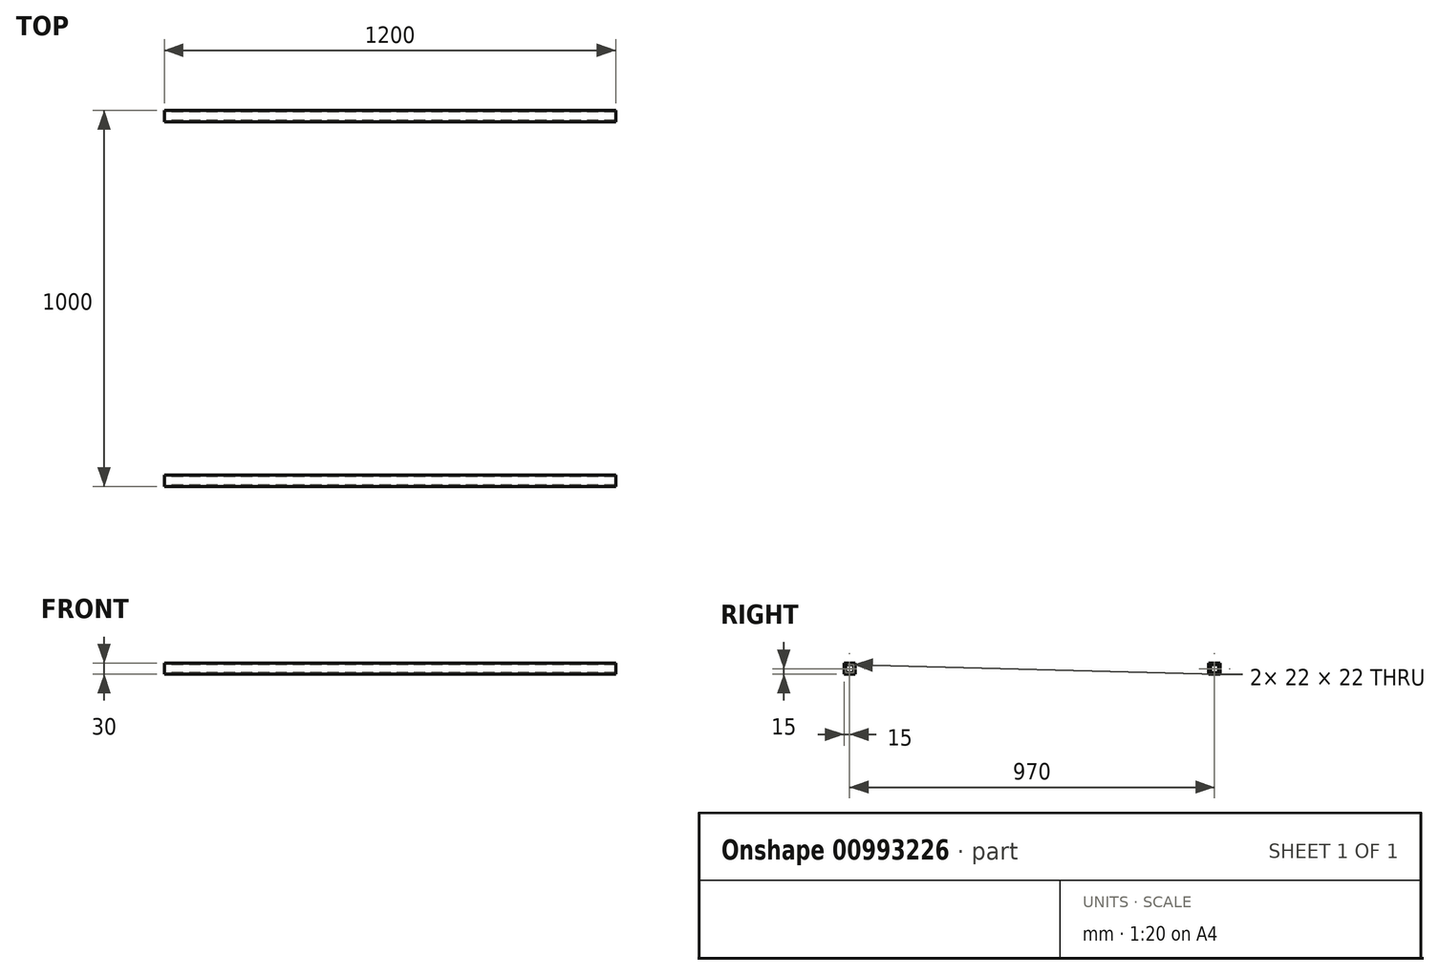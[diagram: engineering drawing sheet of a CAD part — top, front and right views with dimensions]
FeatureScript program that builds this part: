
annotation { "Feature Type Name" : "Feature", "Feature Type Description" : "" }
export const myFeature = defineFeature(function(context is Context, id is Id, definition is map)
    precondition{}
    {
        {
            var Q0;
            Q0=qCreatedBy(makeId("Right.planeOp"),FACE);
            var sketch = newSketch(context, id + "F0", { "sketchPlane" : qUnion([Q0])});
            skLineSegment(sketch, "E0.bottom", {"start": v(-15, 15) * mm, "end": v(15, 15) * mm});
            skLineSegment(sketch, "E0.top", {"start": v(-15, -15) * mm, "end": v(15, -15) * mm});
            skLineSegment(sketch, "E0.left", {"start": v(-15, 15) * mm, "end": v(-15, -15) * mm});
            skLineSegment(sketch, "E0.right", {"start": v(15, 15) * mm, "end": v(15, -15) * mm});
            skLineSegment(sketch, "E1.0", {"start": v(-11, 11) * mm, "end": v(11, 11) * mm});
            skLineSegment(sketch, "E1.1", {"start": v(-11, 11) * mm, "end": v(-11, -11) * mm});
            skLineSegment(sketch, "E1.2", {"start": v(-11, -11) * mm, "end": v(11, -11) * mm});
            skLineSegment(sketch, "E1.3", {"start": v(11, 11) * mm, "end": v(11, -11) * mm});
            skSolve(sketch);
        }
        {
            var Q0;
            Q0=makeQuery(id+"F0.imprint","IMPRINT",FACE,{"disambiguationData":[TD([[makeQuery(id+"F0.imprint","IMPRINT",EDGE,{"derivedFrom":sQuery(id+"F0.wireOp",EDGE,"E0.bottom")}),-1.0]])]});
            extrude(context, id + "F1", {"entities" : qUnion([Q0]), "depth" : 1200 * mm, "offsetDistance" : 25 * mm});
        }
        {
            var Q0;
            Q0=makeQuery(id+"F1.opExtrude","SWEPT_FACE",FACE,{"disambiguationData":[OSD([sQuery(id+"F0.wireOp",EDGE,"E0.right")])]});
            cPlane(context, id + "F2", {"entities" : qUnion([Q0]), "cplaneType" : CPlaneType.OFFSET, "offset" : ((1000 - 60) / 2) * mm, "width" : 150 * mm, "height" : 150 * mm});
        }
        {
            var Q0;
            Q0=makeQuery(id+"F1.opExtrude","SWEPT_BODY",BODY,{"disambiguationData":[OSD([sQuery(id+"F0.wireOp",EDGE,"E0.bottom"),sQuery(id+"F0.wireOp",EDGE,"E0.top"),sQuery(id+"F0.wireOp",EDGE,"E0.left"),sQuery(id+"F0.wireOp",EDGE,"E0.right"),sQuery(id+"F0.wireOp",EDGE,"E1.0"),sQuery(id+"F0.wireOp",EDGE,"E1.1"),sQuery(id+"F0.wireOp",EDGE,"E1.2"),sQuery(id+"F0.wireOp",EDGE,"E1.3")])]});
            var Q1;
            Q1=qCreatedBy(id+"F2.planeOp",FACE);
            mirror(context, id + "F3", {"operationType" : NewBodyOperationType.ADD, "entities" : qUnion([Q0]), "mirrorPlane" : qUnion([Q1])});
        }
    });
